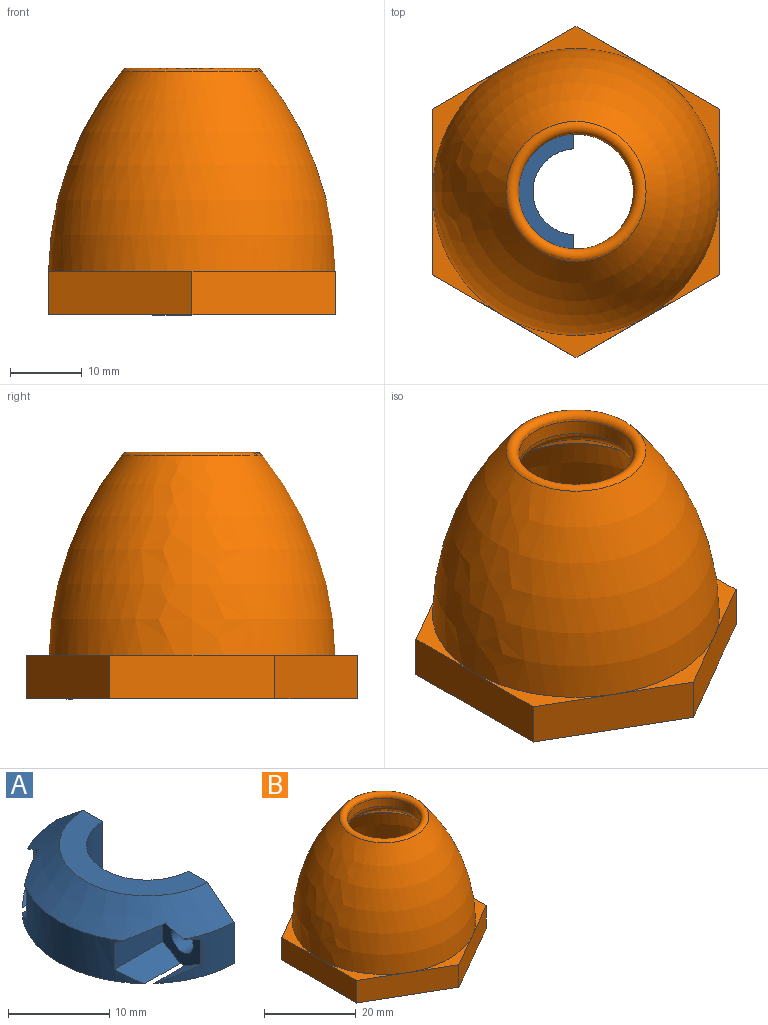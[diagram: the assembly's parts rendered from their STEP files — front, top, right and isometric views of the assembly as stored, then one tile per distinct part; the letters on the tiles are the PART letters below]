
ASSEMBLY  parts=2 mates=1
PART A: 25 faces, bbox 12.4x25x8.3 mm
  f0: cylinder r=12.37mm len=8mm, axis (0,0,-1), area 23.9mm2, adj f3,f4,f8,f18,f20,f22
  f1: cylinder r=12.37mm len=8mm, axis (0,0,-1), area 23.9mm2, adj f3,f4,f7,f11,f14,f15
  f2: cylinder r=12.37mm len=17.13mm, axis (0,0,-1), area 68.7mm2, adj f3,f4,f12,f13,f16,f19,f21,f23
  f3: cone r=12.37mm half-angle=50.8deg, axis (0,0,-1), area 143.3mm2, adj f0,f1,f2,f6,f7,f8,f13,f14
  f4: plane 24.74x12.07mm, normal (0,0,-1), area 174.5mm2, adj f0,f1,f2,f5,f7,f8,f15,f16
  f5: cylinder r=6mm len=11.99mm, axis (0,0,-1), area 146mm2, adj f4,f6,f7,f8
  f6: plane 17.37x8.39mm, normal (0,0,1), area 60.5mm2, adj f3,f5,f7,f8
  f7: plane 8.02x6.4mm, normal (1,0,0), area 38.4mm2, adj f1,f3,f4,f5,f6,f10
  f8: plane 8.02x6.4mm, normal (1,0,0), area 38.4mm2, adj f0,f3,f4,f5,f6,f9
  f9: cylinder r=1.5mm len=3.7mm, axis (1,0,0), area 34.9mm2, adj f8,f24
  f10: cylinder r=1.5mm len=3.7mm, axis (1,0,0), area 34.9mm2, adj f7,f17
  f11: plane 3.18x0.25mm, normal (0,1,0), area 0.8mm2, adj f1,f14,f15,f17
  f12: plane 6.75x3.18mm, normal (0,-1,0), area 21.4mm2, adj f2,f13,f16,f17
  f13: plane 7.01x3mm, normal (0,-0.5,-0.87), area 16mm2, adj f2,f3,f12,f14,f17
  f14: plane 2.81x2.45mm, normal (0,0.5,-0.87), area 6mm2, adj f1,f3,f11,f13,f17
  f15: plane 4.53x2.67mm, normal (0,0.5,0.87), area 7.3mm2, adj f1,f4,f11,f17
  f16: plane 6.82x2.51mm, normal (0,-0.5,0.87), area 16.7mm2, adj f2,f4,f12,f17
  f17: plane 6.18x5.5mm, normal (-1,0,0), area 19.1mm2, adj f4,f10,f11,f12,f13,f14,f15,f16
  f18: plane 3.18x0.25mm, normal (0,-1,0), area 0.8mm2, adj f0,f20,f22,f24
  f19: plane 6.75x3.18mm, normal (0,1,0), area 21.4mm2, adj f2,f21,f23,f24
  f20: plane 2.81x2.45mm, normal (0,-0.5,-0.87), area 6mm2, adj f0,f3,f18,f21,f24
  f21: plane 7.01x3mm, normal (0,0.5,-0.87), area 16mm2, adj f2,f3,f19,f20,f24
  f22: plane 4.53x2.67mm, normal (0,-0.5,0.87), area 7.3mm2, adj f0,f4,f18,f24
  f23: plane 6.82x2.51mm, normal (0,0.5,0.87), area 16.7mm2, adj f2,f4,f19,f24
  f24: plane 6.18x5.5mm, normal (-1,0,0), area 19.1mm2, adj f4,f9,f18,f19,f20,f21,f22,f23
PART B: 31 faces, bbox 40.3x46.5x35.1 mm
  f0: plane 17.32x10mm, normal (0,0,1), area 21.5mm2, adj f13,f14,f27
  f1: plane 20x5.77mm, normal (0,0,1), area 21.5mm2, adj f12,f13,f27
  f2: plane 17.32x10mm, normal (0,0,1), area 21.5mm2, adj f12,f17,f27
  f3: plane 17.32x10mm, normal (0,0,1), area 21.5mm2, adj f16,f17,f27
  f4: plane 20x5.77mm, normal (0,0,1), area 21.5mm2, adj f15,f16,f27
  f5: plane 36x36mm, normal (0,0,1), area 72.3mm2, adj f6,f9,f11,f20,f21,f23,f24
  f6: cylinder r=17.5mm len=8.75mm, axis (0,0,-1), area 0.6mm2, adj f5,f21,f23
  f7: cylinder r=17.5mm len=8.75mm, axis (0,0,-1), area 0.6mm2, adj f10,f19,f22
  f8: plane 0.89x0.51mm, normal (0,-1,0), area 0.2mm2, adj f9,f11,f19,f21
  f9: bspline ~38.52x33.36mm, area 91.7mm2, adj f5,f8,f10,f19,f20,f21
  f10: bspline ~40.41x35mm, area 376.5mm2, adj f7,f9,f11,f19,f20,f22
  f11: cylinder r=17.5mm len=35mm, axis (0,0,-1), area 237.7mm2, adj f5,f8,f10,f19,f20,f21
  f12: plane 20x11.55mm, normal (0.5,0.87,0), area 138.6mm2, adj f1,f2,f13,f17,f19
  f13: plane 20x11.55mm, normal (-0.5,0.87,0), area 138.6mm2, adj f0,f1,f12,f14,f19
  f14: plane 23.09x6mm, normal (-1,0,0), area 138.6mm2, adj f0,f13,f15,f18,f19
  f15: plane 20x11.55mm, normal (-0.5,-0.87,0), area 138.6mm2, adj f4,f14,f16,f18,f19
  f16: plane 20x11.55mm, normal (0.5,-0.87,0), area 138.6mm2, adj f3,f4,f15,f17,f19
  f17: plane 23.09x6mm, normal (1,0,0), area 138.6mm2, adj f2,f3,f12,f16,f19
  f18: plane 17.32x10mm, normal (0,0,1), area 21.5mm2, adj f14,f15,f27
  f19: plane 46.45x40.27mm, normal (0,0,-1), area 440.1mm2, adj f7,f8,f9,f10,f11,f12,f13,f14
  f20: plane 0.89x0.51mm, normal (0,1,0), area 0.2mm2, adj f5,f9,f10,f11
  f21: bspline ~40.41x35mm, area 375.8mm2, adj f5,f6,f8,f9,f11,f23
  f22: plane 0.25x0.13mm, normal (1,0,0), area 0mm2, adj f7,f10,f19
  f23: plane 0.25x0.13mm, normal (1,0,0), area 0mm2, adj f5,f6,f21
  f24: revolved ~36x36mm, area 4287.8mm2, adj f5
  f25: cone r=8mm half-angle=49.1deg, axis (0,0,-1), area 322.2mm2, adj f29,f30
  f26: cylinder r=8mm len=16mm, axis (0,0,-1), area 106.2mm2, adj f28,f29
  f27: revolved ~40x40mm, area 6273.4mm2, adj f0,f1,f2,f3,f4,f18,f28
  f28: torus R=9mm, axis (0,0,1), area 134.9mm2, adj f26,f27
  f29: torus R=10mm, axis (0,0,1), area 88.8mm2, adj f25,f26
  f30: torus R=11.72mm, axis (0,0,-1), area 27.7mm2, adj f25
PLACE A rot(axis=(1,0,0),180deg) t=(0,0,14.14)mm
PLACE B t=(0,0,-6)mm
MATE slider B.f25 <-> A.f0  axis (0,0,-1) through (0,0,14.84)mm
